# Revit family: PRD_AR_FlshCntrlDvcs_F5SmartUrinalUnit_ACEF3003
name_source: partatom
category: Plumbing Fixtures
units: mm (PartAtom-declared; Revit-internal decimal feet)

## family parameters
Always vertical = Yes
Cut with Voids When Loaded = No
Enable Cutting in Views = No
Maintain Annotation Orientation = No
OmniClass Number = 23.65.55.14.17
OmniClass Title = Adjusting/Controlling Valves for Liquid Services
Part Type = Normal
Room Calculation Point = No
Round Connector Dimension = Use Diameter
Shared = No
Work Plane-Based = No

## types (1)
- ACEF3003
    AssetType = Fixed
    BIMObjectName = PRD_AR_FlushControlDevices_F5SmartUrinalUnit_ACEF3003
    BodyMaterial = PRD_AR_Plastic_White
    Category = Pr_75_50_46_31, Flush control devices
    CloseOffRating = 0.0 Pa
    Default Elevation = 0 mm  [stored 0 ft]
    Description = F5 smart urinal unit for installation behind a single urinal made of CMPX539 stainless steel. Water path pre-assembled with hose for water connection, locking and solenoid valve. Control unit in sealed plastic box for wireless communication with the F5 smart urinal sensor. Either for battery operation with 6 V lithium battery (CR-P2) per control unit or separate power supply via power supply unit 6.75 V/12 V DC. Battery compartment including battery or power supply unit with extension cable must be ordered separately.
    DurationUnit = year
    Export Type to IFC As = IfcValveType
    Features = Control unit in sealed plastic box for wireless communication with the F5 smart urinal sensor.  Battery compartment including battery or power supply unit with extension cable must be ordered separately.
    FlowCoefficient = 0
    FlushingRate = 0.0 L/s
    HasIntegralShutOffDevice = No
    IfcExportAs = IfcValveType
    IfcExportType = FLUSHING
    IsHighPressure = No
    Manufacturer = KWC Group Management AG
    ManufacturerName = KWC Group Management AG
    ManufacturerURL = www.kwc-professional.com
    Model = ACEF3003
    ModelNumber = 2030070859
    ModelReference = ACEF3003
    NBSDescription = Flush control devices
    NBSReference = 90-15-35/470
    Name = F5 Smart urinal unit ACEF3003
    NominalDepth = 0 mm  [stored 0 ft]
    NominalHeight = 0 mm  [stored 0 ft]
    NominalWidth = 0 mm  [stored 0 ft]
    ProductInformation = http://pim.kwc.com
    Quantity = 1
    QuantityUom = piece
    Size = 0
    Status = New
    TestPressure = 0.0 Pa
    Type IFC Predefined Type = FLUSHING
    URL = www.kwc-professional.com
    Uniclass2015Code = Pr_75_50_46_31
    Uniclass2015Title = Flush control devices
    Uniclass2015Version = Products v1.32
    ValveMechanism = OTHER
    ValveOperation = OTHER
    ValvePattern = OTHER
    Version = 1
    WarrantyDurationUnit = year
    WorkingPressure = 0.0 Pa

note: [stored X ft] marks values corroborated as IEEE doubles in the binary element streams (Revit-internal decimal feet)

## geometry (parser evidence)
native form markers: Sweep x5
no freeform markers — native parametric forms only
